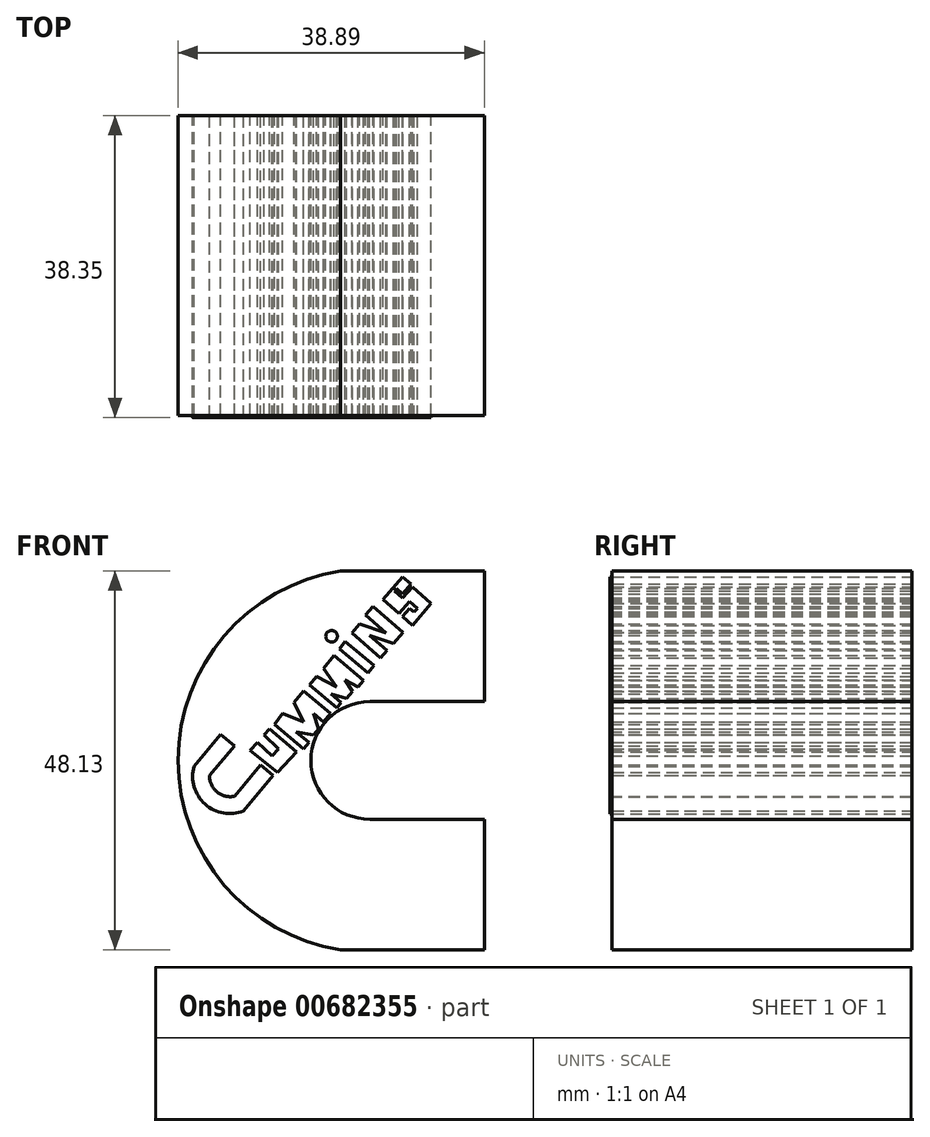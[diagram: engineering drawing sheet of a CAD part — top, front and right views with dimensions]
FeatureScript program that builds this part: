
annotation { "Feature Type Name" : "Feature", "Feature Type Description" : "" }
export const myFeature = defineFeature(function(context is Context, id is Id, definition is map)
    precondition{}
    {
        {
            var Q0;
            Q0=qCreatedBy(makeId("Front.planeOp"),FACE);
            var sketch = newSketch(context, id + "F0", { "sketchPlane" : qUnion([Q0])});
            skLineSegment(sketch, "E0", {"start": v(0, 48.13) * mm, "end": v(-18.26, 48.13) * mm});
            skLineSegment(sketch, "E1", {"start": v(-18.26, 0) * mm, "end": v(0, 0) * mm});
            skLineSegment(sketch, "E2", {"start": v(0, 0) * mm, "end": v(0, 16.59) * mm});
            skLineSegment(sketch, "E3", {"start": v(0, 16.59) * mm, "end": v(-14.53, 16.59) * mm});
            skLineSegment(sketch, "E4", {"start": v(-14.53, 31.54) * mm, "end": v(0, 31.54) * mm});
            skLineSegment(sketch, "E5", {"start": v(0, 31.54) * mm, "end": v(0, 48.13) * mm});
            skArc(sketch, "E6", {"start": v(-18.26, 48.13) * mm, "mid": v(-38.89, 24.06) * mm, "end": v(-18.26, 0) * mm});
            skArc(sketch, "E7", {"start": v(-14.53, 31.54) * mm, "mid": v(-22.01, 24.06) * mm, "end": v(-14.53, 16.59) * mm});
            skPoint(sketch, "E8", {"position": v(-22.01, 24.06) * mm});
            skPoint(sketch, "E9", {"position": v(-38.89, 24.06) * mm});
            skSolve(sketch);
        }
        {
            var Q0;
            Q0=qCreatedBy(makeId("Front.planeOp"),FACE);
            var sketch = newSketch(context, id + "F1", { "sketchPlane" : qUnion([Q0])});
            skLineSegment(sketch, "E10", {"start": v(-36.87, 23.31) * mm, "end": v(-33.5, 27.36) * mm});
            skLineSegment(sketch, "E11", {"start": v(-33.5, 27.36) * mm, "end": v(-31.74, 25.9) * mm});
            skLineSegment(sketch, "E12", {"start": v(-31.74, 25.9) * mm, "end": v(-34.89, 22.13) * mm});
            skLineSegment(sketch, "E13", {"start": v(-31.74, 19.52) * mm, "end": v(-28.43, 23.5) * mm});
            skLineSegment(sketch, "E14", {"start": v(-28.43, 23.5) * mm, "end": v(-26.8, 22.13) * mm});
            skLineSegment(sketch, "E15", {"start": v(-26.8, 22.13) * mm, "end": v(-30.55, 17.63) * mm});
            skArc(sketch, "E16", {"start": v(-36.87, 23.31) * mm, "mid": v(-35.46, 18.52) * mm, "end": v(-30.55, 17.63) * mm});
            skArc(sketch, "E17", {"start": v(-34.89, 22.13) * mm, "mid": v(-33.95, 20.06) * mm, "end": v(-31.74, 19.52) * mm});
            skLineSegment(sketch, "E18", {"start": v(-29.74, 25.36) * mm, "end": v(-28.83, 26.35) * mm});
            skLineSegment(sketch, "E19", {"start": v(-28.83, 26.35) * mm, "end": v(-26.96, 24.63) * mm});
            skLineSegment(sketch, "E20", {"start": v(-26.96, 24.63) * mm, "end": v(-26.11, 25.55) * mm});
            skLineSegment(sketch, "E21", {"start": v(-26.11, 25.55) * mm, "end": v(-28, 27.28) * mm});
            skLineSegment(sketch, "E22", {"start": v(-28, 27.28) * mm, "end": v(-27.28, 28.05) * mm});
            skLineSegment(sketch, "E23", {"start": v(-27.28, 28.05) * mm, "end": v(-23.82, 25.17) * mm});
            skLineSegment(sketch, "E24", {"start": v(-23.82, 25.17) * mm, "end": v(-26.25, 22.52) * mm});
            skLineSegment(sketch, "E25", {"start": v(-26.25, 22.52) * mm, "end": v(-29.74, 25.36) * mm});
            skLineSegment(sketch, "E26", {"start": v(-26.65, 28.63) * mm, "end": v(-22.95, 25.55) * mm});
            skLineSegment(sketch, "E27", {"start": v(-22.95, 25.55) * mm, "end": v(-22.28, 26.35) * mm});
            skLineSegment(sketch, "E28", {"start": v(-22.28, 26.35) * mm, "end": v(-23.88, 27.69) * mm});
            skLineSegment(sketch, "E29", {"start": v(-23.88, 27.69) * mm, "end": v(-21.7, 27.28) * mm});
            skLineSegment(sketch, "E30", {"start": v(-21.7, 27.28) * mm, "end": v(-21.05, 28.05) * mm});
            skLineSegment(sketch, "E31", {"start": v(-21.05, 28.05) * mm, "end": v(-21.7, 30.02) * mm});
            skLineSegment(sketch, "E32", {"start": v(-21.7, 30.02) * mm, "end": v(-20.42, 28.95) * mm});
            skLineSegment(sketch, "E33", {"start": v(-20.42, 28.95) * mm, "end": v(-19.53, 30.02) * mm});
            skLineSegment(sketch, "E34", {"start": v(-19.53, 30.02) * mm, "end": v(-22.95, 32.87) * mm});
            skLineSegment(sketch, "E35", {"start": v(-22.95, 32.87) * mm, "end": v(-24.15, 31.43) * mm});
            skLineSegment(sketch, "E36", {"start": v(-24.15, 31.43) * mm, "end": v(-22.95, 28.95) * mm});
            skLineSegment(sketch, "E37", {"start": v(-22.95, 28.95) * mm, "end": v(-25.64, 30.02) * mm});
            skLineSegment(sketch, "E38", {"start": v(-25.64, 30.02) * mm, "end": v(-26.65, 28.63) * mm});
            skLineSegment(sketch, "E39", {"start": v(-22.17, 33.64) * mm, "end": v(-18.72, 30.76) * mm});
            skLineSegment(sketch, "E40", {"start": v(-18.72, 30.76) * mm, "end": v(-18.17, 31.43) * mm});
            skLineSegment(sketch, "E41", {"start": v(-18.17, 31.43) * mm, "end": v(-19.44, 32.49) * mm});
            skLineSegment(sketch, "E42", {"start": v(-19.44, 32.49) * mm, "end": v(-17.47, 31.96) * mm});
            skPoint(sketch, "E42.endSnap0", {"position": v(-18.8, 31.96) * mm});
            skLineSegment(sketch, "E43", {"start": v(-17.47, 31.96) * mm, "end": v(-16.76, 32.81) * mm});
            skLineSegment(sketch, "E44", {"start": v(-16.76, 32.81) * mm, "end": v(-17.71, 34.28) * mm});
            skLineSegment(sketch, "E45", {"start": v(-17.71, 34.28) * mm, "end": v(-16.04, 33.4) * mm});
            skLineSegment(sketch, "E46", {"start": v(-16.04, 33.4) * mm, "end": v(-15.33, 34.26) * mm});
            skLineSegment(sketch, "E47", {"start": v(-15.33, 34.26) * mm, "end": v(-19.08, 37.38) * mm});
            skLineSegment(sketch, "E48", {"start": v(-19.08, 37.38) * mm, "end": v(-20.42, 35.78) * mm});
            skLineSegment(sketch, "E49", {"start": v(-20.42, 35.78) * mm, "end": v(-18.75, 33.4) * mm});
            skLineSegment(sketch, "E50", {"start": v(-18.75, 33.4) * mm, "end": v(-21.3, 34.76) * mm});
            skLineSegment(sketch, "E51", {"start": v(-21.3, 34.76) * mm, "end": v(-22.17, 33.64) * mm});
            skLineSegment(sketch, "E52", {"start": v(-18.4, 38.2) * mm, "end": v(-14.77, 35.18) * mm});
            skLineSegment(sketch, "E53", {"start": v(-14.77, 35.18) * mm, "end": v(-13.98, 36.12) * mm});
            skLineSegment(sketch, "E54", {"start": v(-13.98, 36.12) * mm, "end": v(-17.66, 39.19) * mm});
            skLineSegment(sketch, "E55", {"start": v(-17.66, 39.19) * mm, "end": v(-18.4, 38.2) * mm});
            skPoint(sketch, "E56.startSnap0", {"position": v(-20.02, 34.08) * mm});
            skCircle(sketch, "E57", {"center": v(-19.4, 39.84) * mm, "radius": 0.74 * mm});
            skLineSegment(sketch, "E58", {"start": v(-16.82, 40.29) * mm, "end": v(-13.17, 37.1) * mm});
            skLineSegment(sketch, "E59", {"start": v(-13.17, 37.1) * mm, "end": v(-12.35, 38.04) * mm});
            skLineSegment(sketch, "E60", {"start": v(-12.35, 38.04) * mm, "end": v(-14.55, 39.97) * mm});
            skLineSegment(sketch, "E61", {"start": v(-14.55, 39.97) * mm, "end": v(-11.52, 38.93) * mm});
            skLineSegment(sketch, "E62", {"start": v(-11.52, 38.93) * mm, "end": v(-10.3, 40.32) * mm});
            skLineSegment(sketch, "E63", {"start": v(-10.3, 40.32) * mm, "end": v(-14.1, 43.65) * mm});
            skLineSegment(sketch, "E64", {"start": v(-14.1, 43.65) * mm, "end": v(-15.07, 42.55) * mm});
            skLineSegment(sketch, "E65", {"start": v(-15.07, 42.55) * mm, "end": v(-12.48, 40.29) * mm});
            skLineSegment(sketch, "E66", {"start": v(-12.48, 40.29) * mm, "end": v(-15.83, 41.43) * mm});
            skLineSegment(sketch, "E67", {"start": v(-15.83, 41.43) * mm, "end": v(-16.82, 40.29) * mm});
            skLineSegment(sketch, "E68", {"start": v(-10.4, 42.34) * mm, "end": v(-9.49, 43.4) * mm});
            skLineSegment(sketch, "E69", {"start": v(-9.49, 43.4) * mm, "end": v(-8.9, 42.9) * mm});
            skLineSegment(sketch, "E70", {"start": v(-8.9, 42.9) * mm, "end": v(-8.48, 43.4) * mm});
            skLineSegment(sketch, "E71", {"start": v(-8.48, 43.4) * mm, "end": v(-9.49, 44.27) * mm});
            skLineSegment(sketch, "E72", {"start": v(-9.49, 44.27) * mm, "end": v(-10.82, 42.73) * mm});
            skLineSegment(sketch, "E73", {"start": v(-10.82, 42.73) * mm, "end": v(-12.86, 44.5) * mm});
            skLineSegment(sketch, "E74", {"start": v(-12.86, 44.5) * mm, "end": v(-10.36, 47.4) * mm});
            skLineSegment(sketch, "E75", {"start": v(-10.4, 42.34) * mm, "end": v(-9.13, 41.24) * mm});
            skLineSegment(sketch, "E76", {"start": v(-9.13, 41.24) * mm, "end": v(-6.77, 43.98) * mm});
            skLineSegment(sketch, "E77", {"start": v(-10.36, 47.4) * mm, "end": v(-9.29, 46.46) * mm});
            skLineSegment(sketch, "E78", {"start": v(-9.29, 46.46) * mm, "end": v(-10.36, 45.22) * mm});
            skLineSegment(sketch, "E79", {"start": v(-10.36, 45.22) * mm, "end": v(-11.14, 45.9) * mm});
            skLineSegment(sketch, "E80", {"start": v(-11.14, 45.9) * mm, "end": v(-11.4, 45.59) * mm});
            skLineSegment(sketch, "E81", {"start": v(-11.4, 45.59) * mm, "end": v(-10.36, 44.69) * mm});
            skLineSegment(sketch, "E82", {"start": v(-10.36, 44.69) * mm, "end": v(-9.14, 46.1) * mm});
            skLineSegment(sketch, "E83", {"start": v(-9.14, 46.1) * mm, "end": v(-6.77, 43.98) * mm});
            skSolve(sketch);
        }
        {
            var Q0;
            Q0=qSketchRegion(id+"F1",true);
            extrude(context, id + "F2", {"entities" : qUnion([Q0]), "depth" : 38.35 * mm});
        }
        {
            var Q0;
            Q0=qSketchRegion(id+"F0",true);
            extrude(context, id + "F3", {"entities" : qUnion([Q0]), "depth" : 38.1 * mm});
        }
    });
